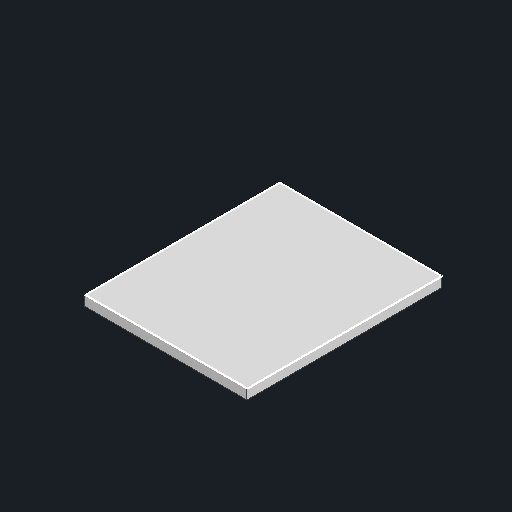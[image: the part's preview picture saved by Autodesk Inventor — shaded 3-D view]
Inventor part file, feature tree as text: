
AUTODESK INVENTOR PART (.ipt)
format: ipt  version: 2022 (Build 260153070, 153G)  size: 91,648 bytes
history: native  units: mm
features: other x1, sketch x1, extrude x1
ambient origin geometry x8: Origin, YZ Plane, XZ Plane, XY Plane, X Axis, Y Axis, Z Axis, Center Point
bodies: Body1 (feature_tree)
feature tree (3):
  other  "Твердое тело1"
  sketch  "Эскиз1"
  extrude  "Выдавливание1"  Depth=250.0mm
